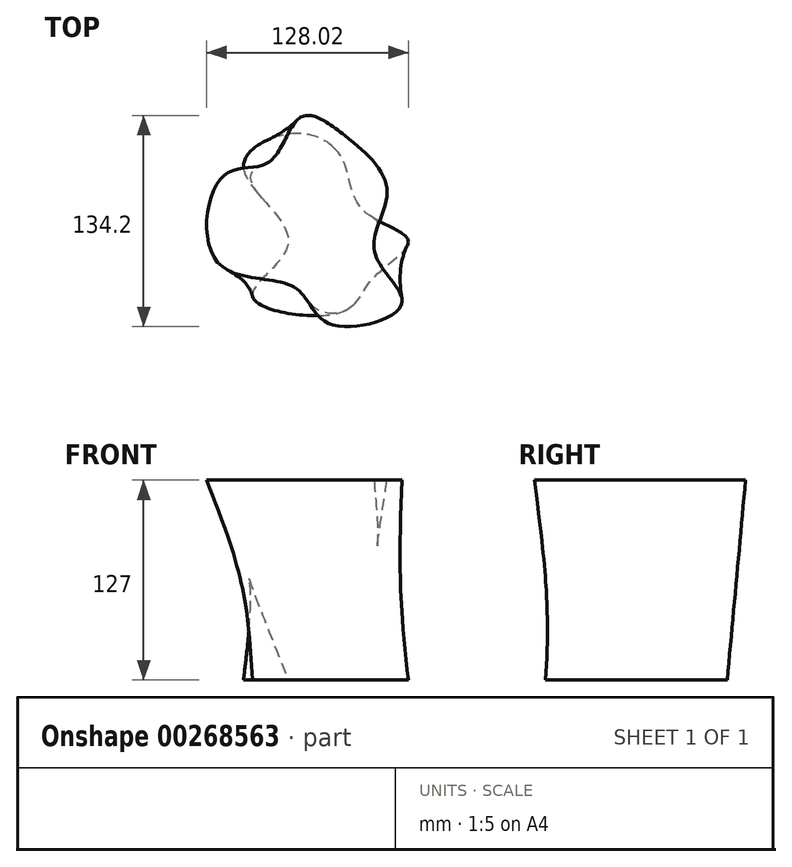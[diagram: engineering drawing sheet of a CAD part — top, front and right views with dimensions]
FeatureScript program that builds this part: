
annotation { "Feature Type Name" : "Feature", "Feature Type Description" : "" }
export const myFeature = defineFeature(function(context is Context, id is Id, definition is map)
    precondition{}
    {
        {
            var Q0;
            Q0=qCreatedBy(makeId("Top.planeOp"),FACE);
            var sketch = newSketch(context, id + "F0", { "sketchPlane" : qUnion([Q0])});
            skFitSpline(sketch, "E0", {"points": [v(14.52, 28.25) * mm, v(-16.41, 44.34) * mm, v(-48.3, 22.57) * mm, v(-19.88, -24.78) * mm, v(-42.6, -58.86) * mm, v(13.18, -69.3) * mm, v(33.43, -48.02) * mm, v(56.25, -23.66) * mm, v(27.54, -4.18) * mm, v(14.52, 28.25) * mm]});
            skSolve(sketch);
        }
        {
            var Q0;
            Q0=qCreatedBy(makeId("Top.planeOp"),FACE);
            cPlane(context, id + "F1", {"entities" : qUnion([Q0]), "cplaneType" : CPlaneType.OFFSET, "offset" : 127 * mm, "width" : 152.4 * mm, "height" : 152.4 * mm});
        }
        {
            var Q0;
            Q0=qCreatedBy(id+"F1.planeOp",FACE);
            var sketch = newSketch(context, id + "F2", { "sketchPlane" : qUnion([Q0])});
            skFitSpline(sketch, "E1", {"points": [v(16.1, 43.08) * mm, v(-12, 54.76) * mm, v(-32.2, 26.35) * mm, v(-61.23, 17.52) * mm, v(-64.7, -37.4) * mm, v(-16.1, -53.18) * mm, v(6.63, -76.54) * mm, v(52.08, -63.91) * mm, v(35.03, -31.4) * mm, v(42.92, 8.05) * mm, v(16.1, 43.08) * mm]});
            skSolve(sketch);
        }
        {
            var Q0;
            Q0=makeQuery(id+"F2.imprint","IMPRINT",FACE,{"disambiguationData":[TD([[makeQuery(id+"F2.imprint","IMPRINT",EDGE,{"derivedFrom":sQuery(id+"F2.wireOp",EDGE,"E1")}),1.0]])]});
            var Q1;
            Q1=makeQuery(id+"F0.imprint","IMPRINT",FACE,{"disambiguationData":[TD([[makeQuery(id+"F0.imprint","IMPRINT",EDGE,{"derivedFrom":sQuery(id+"F0.wireOp",EDGE,"E0")}),1.0]])]});
            loft(context, id + "F3", {"sheetProfilesArray" : [{ "sheetProfileEntities" : qUnion([Q0]) }, { "sheetProfileEntities" : qUnion([Q1]) }]});
        }
    });
